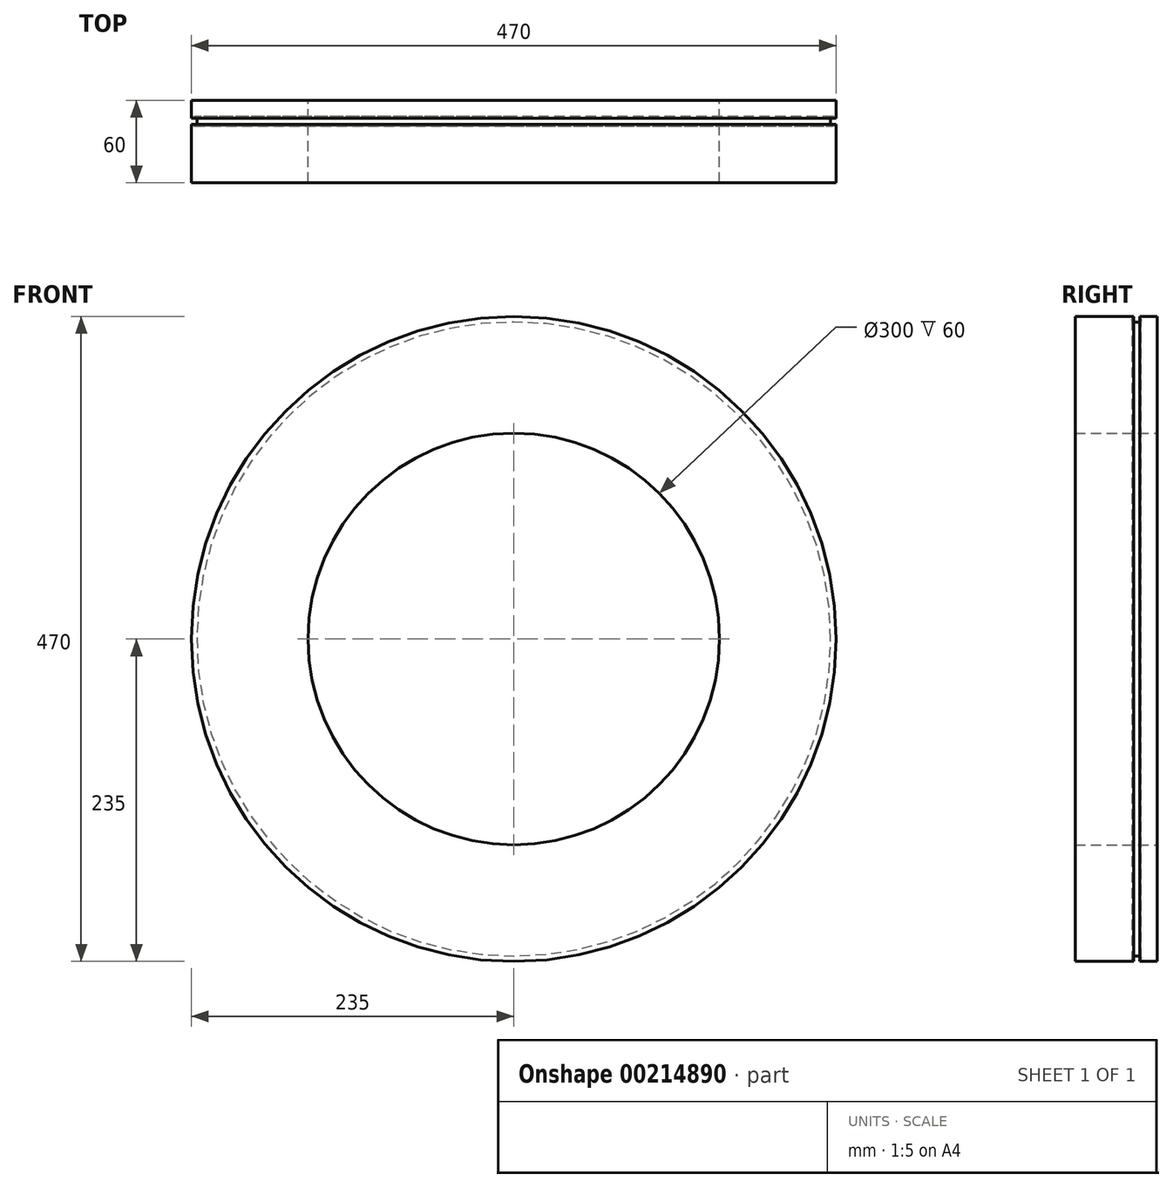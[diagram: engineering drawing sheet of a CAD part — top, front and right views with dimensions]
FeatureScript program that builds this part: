
annotation { "Feature Type Name" : "Feature", "Feature Type Description" : "" }
export const myFeature = defineFeature(function(context is Context, id is Id, definition is map)
    precondition{}
    {
        {
            var Q0;
            Q0=qCreatedBy(makeId("Front.planeOp"),FACE);
            var sketch = newSketch(context, id + "F0", { "sketchPlane" : qUnion([Q0])});
            skCircle(sketch, "E0", {"center": v(0, 0) * mm, "radius": 235 * mm});
            skCircle(sketch, "E1", {"center": v(0, 0) * mm, "radius": 150 * mm});
            skSolve(sketch);
        }
        {
            var Q0;
            Q0=makeQuery(id+"F0.imprint","IMPRINT",FACE,{"disambiguationData":[TD([[makeQuery(id+"F0.imprint","IMPRINT",EDGE,{"derivedFrom":sQuery(id+"F0.wireOp",EDGE,"E0")}),1.0]])]});
            extrude(context, id + "F1", {"entities" : qUnion([Q0]), "depth" : 60 * mm});
        }
        {
            var Q0;
            Q0=qCreatedBy(makeId("Right.planeOp"),FACE);
            var sketch = newSketch(context, id + "F2", { "sketchPlane" : qUnion([Q0])});
            skPoint(sketch, "E2", {"position": v(0, 234.98) * mm});
            skLineSegment(sketch, "E3", {"start": v(-17.45, 234.98) * mm, "end": v(-27.7, 234.98) * mm});
            skLineSegment(sketch, "E4", {"start": v(-17.45, 234.98) * mm, "end": v(-18.45, 233.26) * mm});
            skLineSegment(sketch, "E5", {"start": v(-17.13, 230.98) * mm, "end": v(-15.22, 230.98) * mm});
            skArc(sketch, "E6.filletArc", {"start": v(-18.45, 233.26) * mm, "mid": v(-18.45, 231.74) * mm, "end": v(-17.13, 230.98) * mm});
            skLineSegment(sketch, "E7.MirrorCS", {"start": v(-12.98, 234.98) * mm, "end": v(-11.99, 233.26) * mm});
            skLineSegment(sketch, "E8.MirrorCS", {"start": v(-13.3, 230.98) * mm, "end": v(-15.22, 230.98) * mm});
            skArc(sketch, "E9.MirrorCS", {"start": v(-11.99, 233.26) * mm, "mid": v(-11.99, 231.74) * mm, "end": v(-13.3, 230.98) * mm});
            skLineSegment(sketch, "E10", {"start": v(-12.98, 234.98) * mm, "end": v(-12.98, 236.37) * mm});
            skLineSegment(sketch, "E11", {"start": v(-12.98, 236.37) * mm, "end": v(-17.49, 236.37) * mm});
            skLineSegment(sketch, "E12", {"start": v(-17.49, 236.37) * mm, "end": v(-17.45, 234.98) * mm});
            skLineSegment(sketch, "E13", {"start": v(0, 0) * mm, "end": v(-136.83, 0) * mm});
            skSolve(sketch);
        }
        {
            var Q0;
            Q0 = qSketchRegion(id + "F2", true);
            var Q1;
            Q1=sQuery(id+"F2.wireOp",EDGE,"E13");
            revolve(context, id + "F3", {"operationType" : NewBodyOperationType.REMOVE, "entities" : qUnion([Q0]), "axis" : qUnion([Q1]), "revolveType" : RevolveType.FULL});
        }
    });
